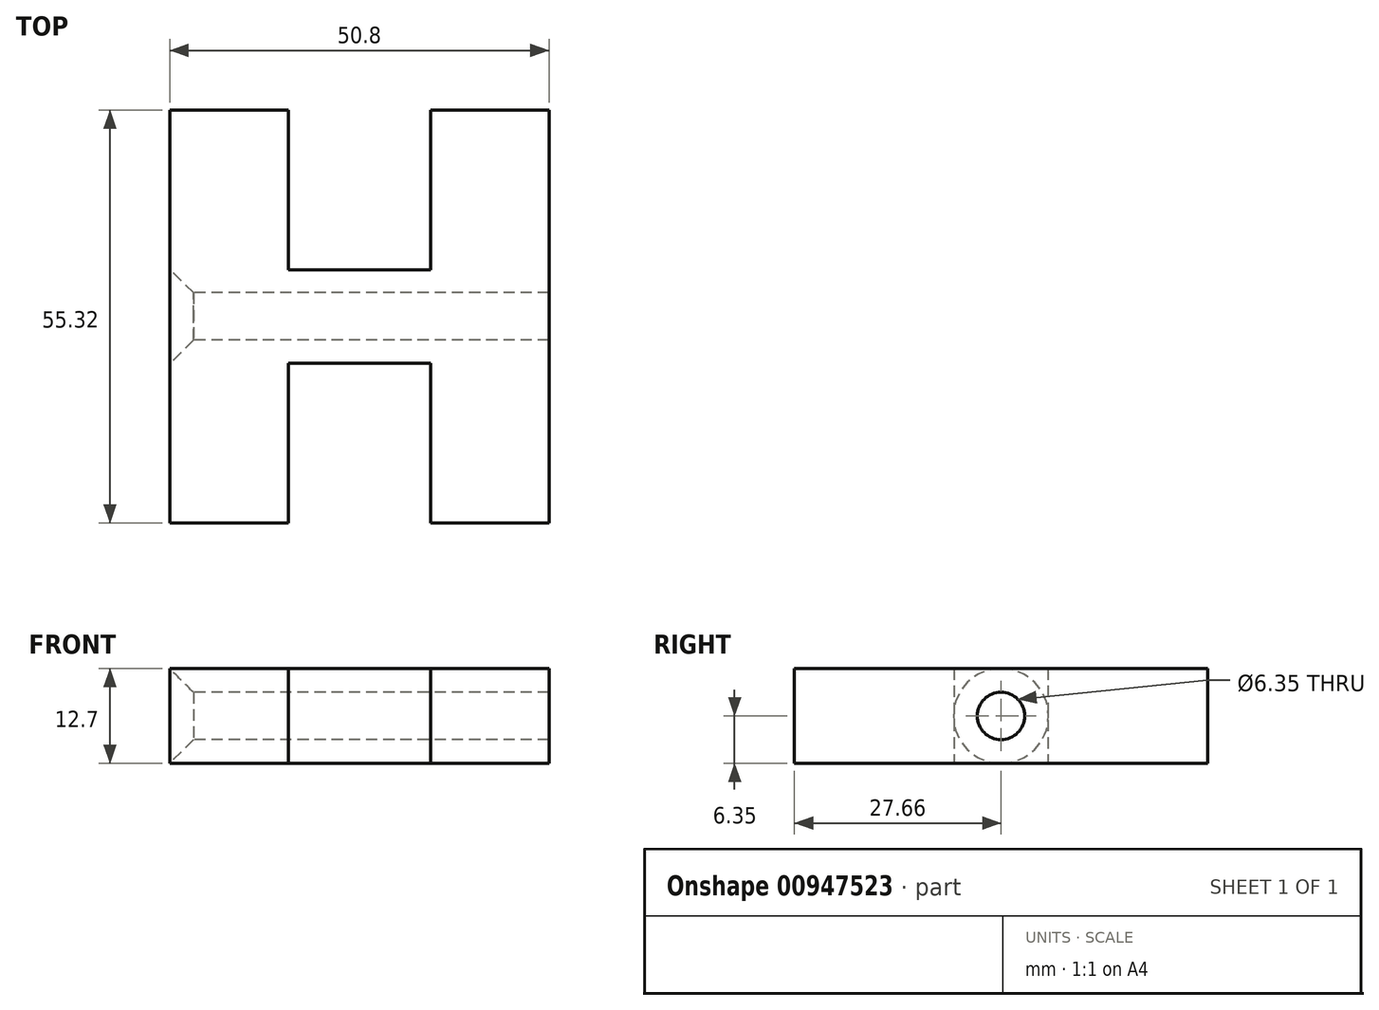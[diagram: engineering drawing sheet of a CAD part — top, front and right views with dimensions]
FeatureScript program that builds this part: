
annotation { "Feature Type Name" : "Feature", "Feature Type Description" : "" }
export const myFeature = defineFeature(function(context is Context, id is Id, definition is map)
    precondition{}
    {
        {
            var Q0;
            Q0=qCreatedBy(makeId("Top.planeOp"),FACE);
            var sketch = newSketch(context, id + "F0", { "sketchPlane" : qUnion([Q0])});
            skLineSegment(sketch, "E0.bottom", {"start": v(-25.4, 27.66) * mm, "end": v(25.4, 27.66) * mm});
            skLineSegment(sketch, "E0.top", {"start": v(-25.4, -27.66) * mm, "end": v(25.4, -27.66) * mm});
            skLineSegment(sketch, "E0.left", {"start": v(-25.4, 27.66) * mm, "end": v(-25.4, -27.66) * mm});
            skLineSegment(sketch, "E0.right", {"start": v(25.4, 27.66) * mm, "end": v(25.4, -27.66) * mm});
            skPoint(sketch, "E0.middle", {"position": v(0, 0) * mm});
            skLineSegment(sketch, "E1.bottom", {"start": v(-9.52, 27.66) * mm, "end": v(9.52, 27.66) * mm});
            skLineSegment(sketch, "E1.top", {"start": v(-9.52, 6.28) * mm, "end": v(9.53, 6.28) * mm});
            skLineSegment(sketch, "E1.left", {"start": v(-9.52, 27.66) * mm, "end": v(-9.52, 6.28) * mm});
            skLineSegment(sketch, "E1.right", {"start": v(9.52, 27.66) * mm, "end": v(9.53, 6.28) * mm});
            skLineSegment(sketch, "E2", {"start": v(0, 30.71) * mm, "end": v(0, -17.14) * mm});
            skPoint(sketch, "E3", {"position": v(0, 6.28) * mm});
            skPoint(sketch, "E4", {"position": v(0, -27.66) * mm});
            skLineSegment(sketch, "E5.MirrorCS", {"start": v(-9.52, -27.66) * mm, "end": v(-9.52, -6.28) * mm});
            skLineSegment(sketch, "E6.MirrorCS", {"start": v(-9.52, -27.66) * mm, "end": v(9.52, -27.66) * mm});
            skLineSegment(sketch, "E7.MirrorCS", {"start": v(9.52, -27.66) * mm, "end": v(9.53, -6.28) * mm});
            skLineSegment(sketch, "E8.MirrorCS", {"start": v(-9.52, -6.28) * mm, "end": v(9.53, -6.28) * mm});
            skSolve(sketch);
        }
        {
            var Q0;
            {var subQ4=sQuery(id+"F0.wireOp",EDGE,"E0.left");Q0=makeQuery(id+"F0.imprint","IMPRINT",FACE,{"disambiguationData":[TD([[makeQuery(id+"F0.imprint","IMPRINT",EDGE,{"derivedFrom":subQ4}),1.0]])]});}
            var Q1;
            {var subQ4=sQuery(id+"F0.wireOp",EDGE,"E0.right");Q1=makeQuery(id+"F0.imprint","IMPRINT",FACE,{"disambiguationData":[TD([[makeQuery(id+"F0.imprint","IMPRINT",EDGE,{"derivedFrom":subQ4}),-1.0]])]});}
            extrude(context, id + "F1", {"entities" : qUnion([Q0, Q1]), "depth" : 12.7 * mm, "offsetDistance" : 25.4 * mm});
        }
        {
            var Q0;
            Q0=makeQuery(id+"F1.opExtrude","SWEPT_FACE",FACE,{"disambiguationData":[OSD([sQuery(id+"F0.wireOp",EDGE,"E0.left")])]});
            var sketch = newSketch(context, id + "F2", { "sketchPlane" : qUnion([Q0])});
            skPoint(sketch, "E9", {"position": v(0, 6.35) * mm});
            skPoint(sketch, "E9.positionSnap0", {"position": v(0, 12.7) * mm});
            skLineSegment(sketch, "E10", {"start": v(0, 12.7) * mm, "end": v(0, 0) * mm, "construction": true});
            skSolve(sketch);
        }
        {
            var Q0;
            Q0=sQuery(id+"F2.wireOp",VERTEX,"E9");
            var Q1;
            Q1=makeQuery(id+"F1.opExtrude","SWEPT_BODY",BODY,{"disambiguationData":[OSD([sQuery(id+"F0.wireOp",EDGE,"E0.bottom"),sQuery(id+"F0.wireOp",EDGE,"E0.top"),sQuery(id+"F0.wireOp",EDGE,"E0.left"),sQuery(id+"F0.wireOp",EDGE,"E0.right"),sQuery(id+"F0.wireOp",EDGE,"E1.top"),sQuery(id+"F0.wireOp",EDGE,"E1.left"),sQuery(id+"F0.wireOp",EDGE,"E1.right"),sQuery(id+"F0.wireOp",EDGE,"E5.MirrorCS"),sQuery(id+"F0.wireOp",EDGE,"E7.MirrorCS"),sQuery(id+"F0.wireOp",EDGE,"E8.MirrorCS")])]});
            hole(context, id + "F3", {"style" : HoleStyle.C_SINK, "endStyle" : HoleEndStyle.THROUGH, "holeDiameter" : 6.35 * mm, "cSinkDiameter" : 12.7 * mm, "cSinkAngle" : 90 * degree, "majorDiameter" : 6.35 * mm, "isTappedThrough" : true, "tappedDepth" : 12.7 * mm, "tapClearance" : 3, "locations" : qUnion([Q0]), "scope" : qUnion([Q1])});
        }
    });
